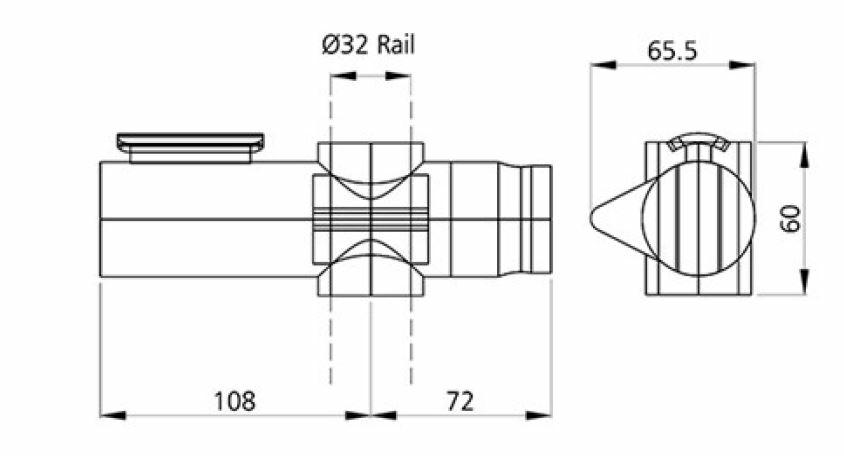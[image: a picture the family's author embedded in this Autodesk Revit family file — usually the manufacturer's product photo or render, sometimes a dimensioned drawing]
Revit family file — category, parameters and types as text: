
# Revit family: rba-bim-rba4110-951
name_source: partatom
category: Plumbing Fixtures
revit_build: Autodesk Revit 2018 (Build: 20170223_1515(x64)
units: mm (PartAtom-declared; Revit-internal decimal feet)

## family parameters
Always vertical = Yes
Cut with Voids When Loaded = No
Part Type = Normal
Room Calculation Point = No
Round Connector Dimension = Use Diameter
Shared = Yes
Work Plane-Based = No

## types (1)
- RBA4110-951
    CW Connection = Yes
    Description = LH T-Rail for Showers, incl Slider & 4 Star Handset and Mixer
    Distance Away from Toilet (default) = 1090 mm  [stored 3.57612 ft]
    Distance Away from Wall (default) = 100 mm  [stored 0.328084 ft]
    HW Connection = Yes
    Manufacturer = RBA Group
    Materials and Finishes = Chrome w/ Stainless Steel Hose
    Model = RBA4110-951
    Modified Issue = 20201019.01
    OFFSET = 1000 mm  [stored 3.28084 ft]
    URL = www.rba.com.au
    Vent Connection = Yes
    Waste Connection = Yes

note: [stored X ft] marks values corroborated as IEEE doubles in the binary element streams (Revit-internal decimal feet)

## geometry (parser evidence)
native form markers: Blend x12, Sweep x22
no freeform markers — native parametric forms only
